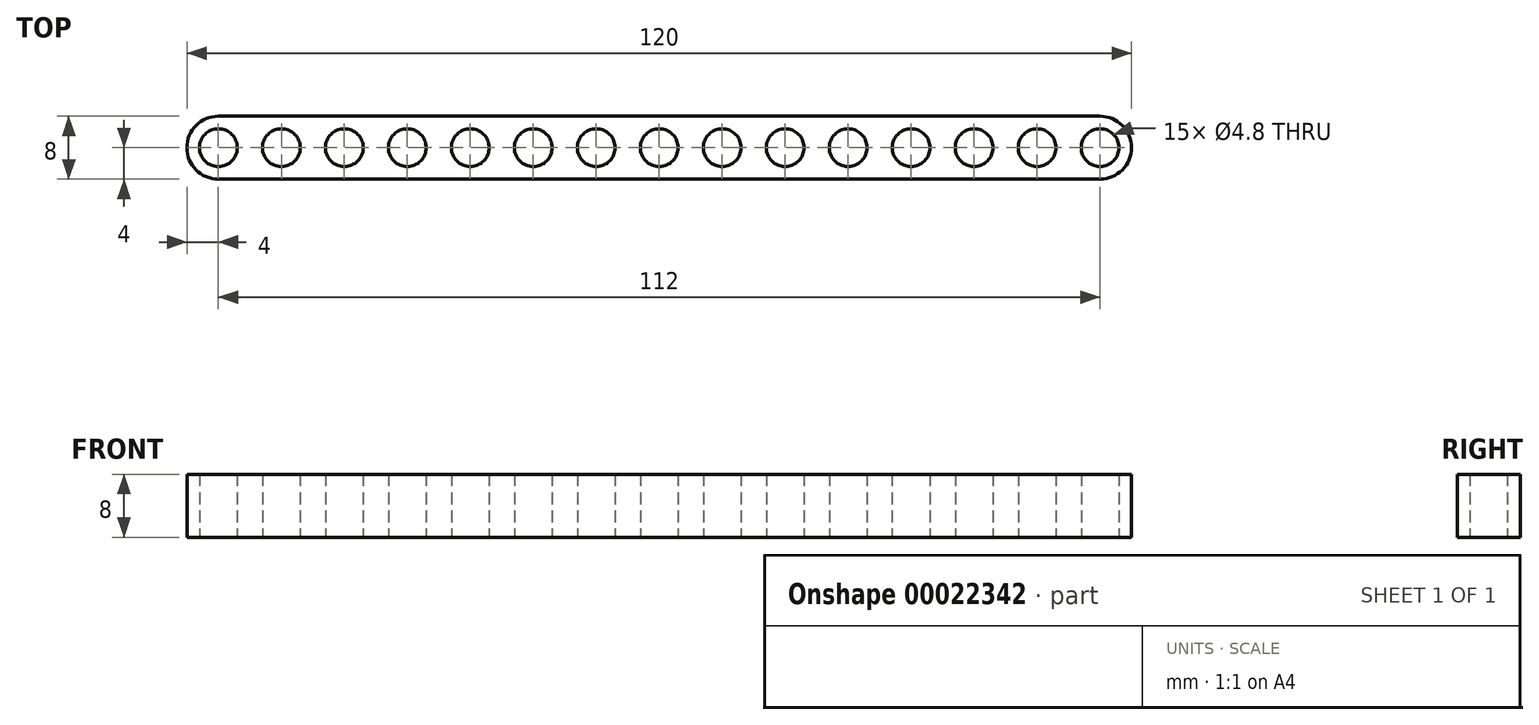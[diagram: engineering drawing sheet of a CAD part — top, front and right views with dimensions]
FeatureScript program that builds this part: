
annotation { "Feature Type Name" : "Feature", "Feature Type Description" : "" }
export const myFeature = defineFeature(function(context is Context, id is Id, definition is map)
    precondition{}
    {
        {
            var Q0;
            Q0=qCreatedBy(makeId("Top.planeOp"),FACE);
            var sketch = newSketch(context, id + "F0", { "sketchPlane" : qUnion([Q0])});
            skCircle(sketch, "E0", {"center": v(0, 0) * mm, "radius": 2.4 * mm});
            skCircle(sketch, "E1.1.0.0", {"center": v(8, 0) * mm, "radius": 2.4 * mm});
            skCircle(sketch, "E1.2.0.0", {"center": v(16, 0) * mm, "radius": 2.4 * mm});
            skCircle(sketch, "E1.3.0.0", {"center": v(24, 0) * mm, "radius": 2.4 * mm});
            skCircle(sketch, "E1.4.0.0", {"center": v(32, 0) * mm, "radius": 2.4 * mm});
            skCircle(sketch, "E1.5.0.0", {"center": v(40, 0) * mm, "radius": 2.4 * mm});
            skCircle(sketch, "E1.6.0.0", {"center": v(48, 0) * mm, "radius": 2.4 * mm});
            skCircle(sketch, "E1.7.0.0", {"center": v(56, 0) * mm, "radius": 2.4 * mm});
            skCircle(sketch, "E1.8.0.0", {"center": v(64, 0) * mm, "radius": 2.4 * mm});
            skCircle(sketch, "E1.9.0.0", {"center": v(72, 0) * mm, "radius": 2.4 * mm});
            skCircle(sketch, "E1.10.0.0", {"center": v(80, 0) * mm, "radius": 2.4 * mm});
            skCircle(sketch, "E1.11.0.0", {"center": v(88, 0) * mm, "radius": 2.4 * mm});
            skCircle(sketch, "E1.12.0.0", {"center": v(96, 0) * mm, "radius": 2.4 * mm});
            skCircle(sketch, "E1.13.0.0", {"center": v(104, 0) * mm, "radius": 2.4 * mm});
            skCircle(sketch, "E1.14.0.0", {"center": v(112, 0) * mm, "radius": 2.4 * mm});
            skLineSegment(sketch, "E1.direction1", {"start": v(0, 0) * mm, "end": v(8, 0) * mm, "construction": true});
            skLineSegment(sketch, "E2", {"start": v(0, 0) * mm, "end": v(112, 0) * mm, "construction": true});
            skLineSegment(sketch, "E3.bottom", {"start": v(0, -4) * mm, "end": v(112, -4) * mm});
            skLineSegment(sketch, "E3.top", {"start": v(0, 4) * mm, "end": v(112, 4) * mm});
            skArc(sketch, "E4", {"start": v(0, 4) * mm, "mid": v(-4, 0) * mm, "end": v(0, -4) * mm});
            skArc(sketch, "E5", {"start": v(112, -4) * mm, "mid": v(116, 0) * mm, "end": v(112, 4) * mm});
            skSolve(sketch);
        }
        {
            var Q0;
            Q0=makeQuery(id+"F0.imprint","IMPRINT",FACE,{"disambiguationData":[TD([[makeQuery(id+"F0.imprint","IMPRINT",EDGE,{"derivedFrom":sQuery(id+"F0.wireOp",EDGE,"E0")}),-1.0]])]});
            extrude(context, id + "F1", {"entities" : qUnion([Q0]), "endBound" : BoundingType.SYMMETRIC, "depth" : 8 * mm});
        }
    });
